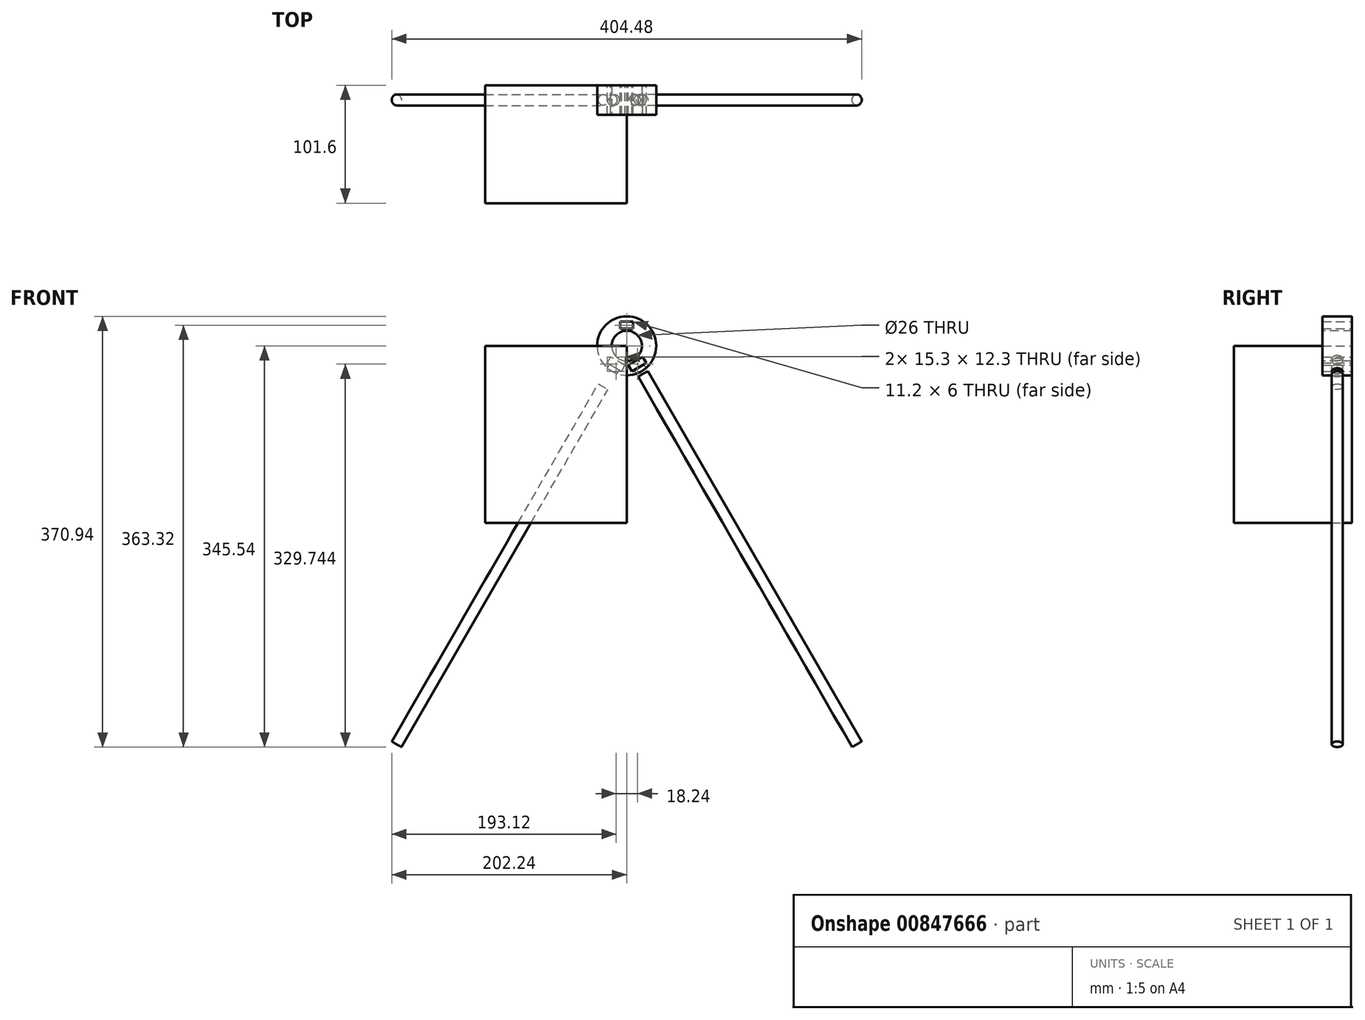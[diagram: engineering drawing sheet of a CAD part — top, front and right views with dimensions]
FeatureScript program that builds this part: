
annotation { "Feature Type Name" : "Feature", "Feature Type Description" : "" }
export const myFeature = defineFeature(function(context is Context, id is Id, definition is map)
    precondition{}
    {
        {
            var Q0;
            Q0=qCreatedBy(makeId("Front.planeOp"),FACE);
            var sketch = newSketch(context, id + "F0", { "sketchPlane" : qUnion([Q0])});
            skCircle(sketch, "E0", {"center": v(0, 0) * mm, "radius": 13 * mm});
            skSolve(sketch);
        }
        {
            var Q0;
            Q0 = qSketchRegion(id + "F0", true);
            extrude(context, id + "F1", {"entities" : qUnion([Q0]), "depth" : 393.7 * mm, "offsetDistance" : 25.4 * mm});
        }
        {
            var Q0;
            Q0=qCreatedBy(makeId("Front.planeOp"),FACE);
            var sketch = newSketch(context, id + "F2", { "sketchPlane" : qUnion([Q0])});
            skCircle(sketch, "E1", {"center": v(0, 0) * mm, "radius": 25.4 * mm});
            skLineSegment(sketch, "E2.bottom", {"start": v(5.6, 14.78) * mm, "end": v(-5.6, 14.78) * mm});
            skLineSegment(sketch, "E2.top", {"start": v(5.6, 20.78) * mm, "end": v(-5.6, 20.78) * mm});
            skLineSegment(sketch, "E2.left", {"start": v(5.6, 14.78) * mm, "end": v(5.6, 20.78) * mm});
            skLineSegment(sketch, "E2.right", {"start": v(-5.6, 14.78) * mm, "end": v(-5.6, 20.78) * mm});
            skPoint(sketch, "E2.middle", {"position": v(0, 17.78) * mm});
            skLineSegment(sketch, "E3", {"start": v(0, 0) * mm, "end": v(29.45, 0) * mm, "construction": true});
            skLineSegment(sketch, "E4", {"start": v(0, 0) * mm, "end": v(12.7, -22) * mm, "construction": true});
            skLineSegment(sketch, "E5", {"start": v(0, 0) * mm, "end": v(-12.7, -22) * mm, "construction": true});
            skLineSegment(sketch, "E6.bottom", {"start": v(16.77, -14.84) * mm, "end": v(4.47, -21.94) * mm});
            skLineSegment(sketch, "E6.top", {"start": v(13.77, -9.65) * mm, "end": v(7.62, -13.2) * mm});
            skLineSegment(sketch, "E6.left", {"start": v(16.77, -14.84) * mm, "end": v(13.77, -9.65) * mm});
            skLineSegment(sketch, "E6.right", {"start": v(4.47, -21.94) * mm, "end": v(1.47, -16.75) * mm});
            skLineSegment(sketch, "E7", {"start": v(7.62, -13.2) * mm, "end": v(1.47, -16.75) * mm});
            skLineSegment(sketch, "E8.bottom", {"start": v(-4.47, -21.94) * mm, "end": v(-16.77, -14.84) * mm});
            skLineSegment(sketch, "E8.top", {"start": v(-1.47, -16.75) * mm, "end": v(-7.62, -13.2) * mm});
            skLineSegment(sketch, "E8.left", {"start": v(-4.47, -21.94) * mm, "end": v(-1.47, -16.75) * mm});
            skLineSegment(sketch, "E8.right", {"start": v(-16.77, -14.84) * mm, "end": v(-13.77, -9.65) * mm});
            skLineSegment(sketch, "E9", {"start": v(-7.62, -13.2) * mm, "end": v(-13.77, -9.65) * mm});
            skSolve(sketch);
        }
        {
            var Q0;
            Q0=makeQuery(id+"F2.imprint","IMPRINT",FACE,{"disambiguationData":[TD([[makeQuery(id+"F2.imprint","IMPRINT",EDGE,{"derivedFrom":sQuery(id+"F2.wireOp",EDGE,"E1")}),1.0]])]});
            extrude(context, id + "F3", {"entities" : qUnion([Q0]), "depth" : 25.4 * mm, "offsetDistance" : 25.4 * mm});
        }
        {
            var Q0;
            Q0=makeQuery(id+"F1.opExtrude","CAP_FACE",FACE,{"disambiguationData":[OSD([sQuery(id+"F0.wireOp",EDGE,"E0")])],"isStart":false});
            extrude(context, id + "F4", {"entities" : qUnion([Q0]), "operationType" : NewBodyOperationType.REMOVE, "oppositeDirection" : true, "depth" : 393.7 * mm, "offsetDistance" : 25.4 * mm});
        }
        {
            var Q0;
            Q0=makeQuery(id+"F3.opExtrude","SWEPT_FACE",FACE,{"disambiguationData":[OSD([sQuery(id+"F2.wireOp",EDGE,"E6.top"),sQuery(id+"F2.wireOp",EDGE,"E7")])]});
            var sketch = newSketch(context, id + "F5", { "sketchPlane" : qUnion([Q0])});
            skCircle(sketch, "E10", {"center": v(0, 12.7) * mm, "radius": 4.76 * mm});
            skLineSegment(sketch, "E11", {"start": v(0, 0.43) * mm, "end": v(0, 25.4) * mm, "construction": true});
            skLineSegment(sketch, "E12", {"start": v(-25.4, 0) * mm, "end": v(-25.4, 25.4) * mm, "construction": true});
            skLineSegment(sketch, "E13", {"start": v(25.4, 25.4) * mm, "end": v(25.4, 0) * mm, "construction": true});
            skLineSegment(sketch, "E14", {"start": v(-25.4, 12.7) * mm, "end": v(25.4, 12.7) * mm, "construction": true});
            skSolve(sketch);
        }
        {
            var Q0;
            Q0 = qSketchRegion(id + "F5", true);
            extrude(context, id + "F6", {"entities" : qUnion([Q0]), "depth" : 381 * mm, "offsetDistance" : 25.4 * mm});
        }
        {
            var Q0;
            Q0 = qSketchRegion(id + "F5", true);
            extrude(context, id + "F7", {"entities" : qUnion([Q0]), "operationType" : NewBodyOperationType.REMOVE, "endBound" : BoundingType.SYMMETRIC, "depth" : 25.4 * mm, "offsetDistance" : 25.4 * mm});
        }
        {
            var Q0;
            Q0=makeQuery(id+"F3.opExtrude","SWEPT_FACE",FACE,{"disambiguationData":[OSD([sQuery(id+"F2.wireOp",EDGE,"E8.top"),sQuery(id+"F2.wireOp",EDGE,"E9")])]});
            var sketch = newSketch(context, id + "F8", { "sketchPlane" : qUnion([Q0])});
            skCircle(sketch, "E15", {"center": v(0, 12.7) * mm, "radius": 4.76 * mm});
            skLineSegment(sketch, "E16.0", {"start": v(7.1, 25.4) * mm, "end": v(0, 25.4) * mm, "construction": true});
            skLineSegment(sketch, "E17.0", {"start": v(-7.1, 25.4) * mm, "end": v(-7.1, 12.7) * mm, "construction": true});
            skLineSegment(sketch, "E18.0", {"start": v(7.1, 25.4) * mm, "end": v(7.1, 0) * mm, "construction": true});
            skLineSegment(sketch, "E19.0", {"start": v(0, 0) * mm, "end": v(-7.1, 0) * mm, "construction": true});
            skLineSegment(sketch, "E20.0", {"start": v(7.1, 0) * mm, "end": v(0, 0) * mm, "construction": true});
            skLineSegment(sketch, "E21", {"start": v(-7.1, 12.7) * mm, "end": v(-7.1, 0) * mm, "construction": true});
            skLineSegment(sketch, "E22", {"start": v(0, 25.4) * mm, "end": v(-7.1, 25.4) * mm, "construction": true});
            skLineSegment(sketch, "E23", {"start": v(0, 25.4) * mm, "end": v(0, 0) * mm, "construction": true});
            skLineSegment(sketch, "E24", {"start": v(-7.1, 12.7) * mm, "end": v(7.1, 12.7) * mm, "construction": true});
            skSolve(sketch);
        }
        {
            var Q0;
            Q0 = qSketchRegion(id + "F8", true);
            extrude(context, id + "F9", {"entities" : qUnion([Q0]), "depth" : 381 * mm, "offsetDistance" : 25.4 * mm});
        }
        {
            var Q0;
            Q0 = qSketchRegion(id + "F8", true);
            extrude(context, id + "F10", {"entities" : qUnion([Q0]), "operationType" : NewBodyOperationType.REMOVE, "depth" : 25.4 * mm, "offsetDistance" : 25.4 * mm});
        }
        {
            var Q0;
            Q0=qCreatedBy(makeId("Front.planeOp"),FACE);
            var sketch = newSketch(context, id + "F11", { "sketchPlane" : qUnion([Q0])});
            skLineSegment(sketch, "E25.bottom", {"start": v(0, 0) * mm, "end": v(-121.92, 0) * mm});
            skLineSegment(sketch, "E25.top", {"start": v(0, -152.4) * mm, "end": v(-121.92, -152.4) * mm});
            skLineSegment(sketch, "E25.left", {"start": v(0, 0) * mm, "end": v(0, -152.4) * mm});
            skLineSegment(sketch, "E25.right", {"start": v(-121.92, 0) * mm, "end": v(-121.92, -152.4) * mm});
            skSolve(sketch);
        }
        {
            var Q0;
            Q0 = qSketchRegion(id + "F11", true);
            extrude(context, id + "F12", {"entities" : qUnion([Q0]), "depth" : 101.6 * mm, "offsetDistance" : 25.4 * mm});
        }
    });
